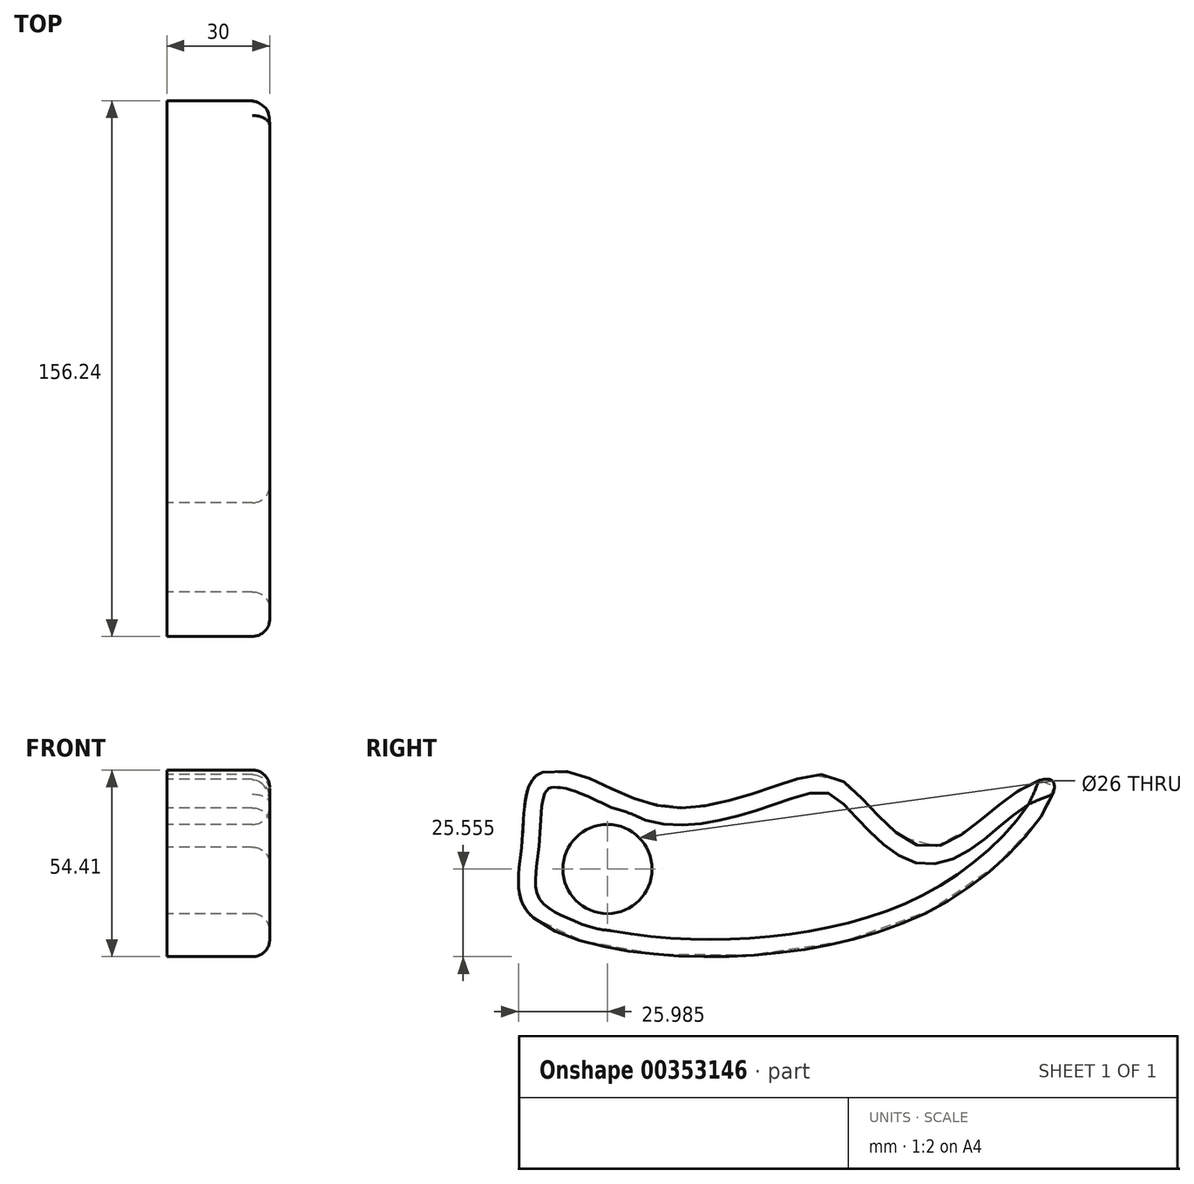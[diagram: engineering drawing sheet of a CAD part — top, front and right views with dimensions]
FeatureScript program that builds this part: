
annotation { "Feature Type Name" : "Feature", "Feature Type Description" : "" }
export const myFeature = defineFeature(function(context is Context, id is Id, definition is map)
    precondition{}
    {
        {
            var Q0;
            Q0=qCreatedBy(makeId("Right.planeOp"),FACE);
            var sketch = newSketch(context, id + "F0", { "sketchPlane" : qUnion([Q0])});
            skFitSpline(sketch, "E0", {"points": [v(0, 0) * mm, v(-3.45, 21.03) * mm, v(0, 40.74) * mm, v(13.03, 41.91) * mm, v(40.38, 32.2) * mm, v(76.55, 40.44) * mm, v(90.97, 39.26) * mm, v(113.9, 20.74) * mm, v(140.08, 36.32) * mm, v(151.55, 39.56) * mm, v(111.26, 0) * mm, v(0, 0) * mm]});
            skCircle(sketch, "E1", {"center": v(21.55, 14.26) * mm, "radius": 13 * mm});
            skSolve(sketch);
        }
        {
            var Q0;
            Q0=makeQuery(id+"F0.imprint","IMPRINT",FACE,{"disambiguationData":[TD([[makeQuery(id+"F0.imprint","IMPRINT",EDGE,{"derivedFrom":sQuery(id+"F0.wireOp",EDGE,"E0")}),-1.0]])]});
            extrude(context, id + "F1", {"entities" : qUnion([Q0]), "depth" : 30 * mm});
        }
        {
            var Q0;
            Q0=makeQuery(id+"F1.opExtrude","CAP_EDGE",EDGE,{"disambiguationData":[OSD([sQuery(id+"F0.wireOp",EDGE,"E1")])],"isStart":false});
            var Q1;
            Q1=makeQuery(id+"F1.opExtrude","CAP_EDGE",EDGE,{"disambiguationData":[OSD([sQuery(id+"F0.wireOp",EDGE,"E0")])],"isStart":false});
            fillet(context, id + "F2", {"entities" : qUnion([Q0, Q1]), "radius" : 5 * mm, "tangentPropagation" : true, "allowEdgeOverflow" : false});
        }
    });
